# Revit family: НЕВАТОМ_Козырек VR-KP, версия 1
name_source: partatom
category: Оборудование
revit_build: Autodesk Revit 2017 (Build: 20170118_1100(x64)
units: mm (PartAtom-declared; Revit-internal decimal feet)

## family parameters
Всегда вертикально = Нет
На основе рабочей плоскости = Нет
Общий = Нет
При загрузке вырезать с полостями = Нет
Размер круглого соединителя = Использовать диаметр
Тип детали = Нормальный
Точка расчета площади = Нет

## types (12) — shared parameters
ADSK_Единица измерения = шт.
ADSK_Завод-изготовитель = НЕВАТОМ
ADSK_Количество = 1
ADSK_Материал наименование = сталь оцинкованная
Nevatom_URL = https://t.me
a = 5 мм
f1 = 5 мм
l = 60 мм

## per-type parameters (varying)
| type | A+60 | ADSK_Марка | ADSK_Наименование | L | l1 | А | С | С+60 |
| Козырек VR-KP 250-0,55/3000 | 205 мм | VR-KP 250-0,55/3000 | Козырек VR-KP 250-0,55/3000 | 350 мм | 100 мм | 145 мм | 390 мм | 450 мм |
| Козырек VR-KP 710-3/1000 | 457 мм | VR-KP 710-3/1000 | Козырек VR-KP 710-3/1000 | 650 мм | 186 мм | 397 мм | 990 мм | 1050 мм |
| Козырек VR-KP 280-0,75/3000 | 240 мм | VR-KP 280-0,75/3000 | Козырек VR-KP 280-0,75/3000 | 350 мм | 100 мм | 180 мм | 390 мм | 450 мм |
| Козырек VR-KP 315-1,5/3000 | 258 мм | VR-KP 315-1,5/3000 | Козырек VR-KP 315-1,5/3000 | 400 мм | 114 мм | 198 мм | 490 мм | 550 мм |
| Козырек VR-KP 355-2,2/3000 | 282 мм | VR-KP 355-2,2/3000 | Козырек VR-KP 355-2,2/3000 | 400 мм | 114 мм | 222 мм | 490 мм | 550 мм |
| Козырек VR-KP 400-0,55/1500 | 283 мм | VR-KP 400-0,55/1500 | Козырек VR-KP 400-0,55/1500 | 475 мм | 136 мм | 223 мм | 640 мм | 700 мм |
| Козырек VR-KP 450-0,75/1500 | 304 мм | VR-KP 400-0,55/1500 | Козырек VR-KP 400-0,55/1500 | 475 мм | 136 мм | 244 мм | 640 мм | 700 мм |
| Козырек VR-KP 500-0,37/1000 | 323 мм | VR-KP 500-0,37/1000 | Козырек VR-KP 500-0,37/1000 | 550 мм | 157 мм | 263 мм | 790 мм | 850 мм |
| Козырек VR-KP 500-1,5/1500 | 343 мм | VR-KP 500-1,5/1500 | Козырек VR-KP 500-1,5/1500 | 550 мм | 157 мм | 283 мм | 790 мм | 850 мм |
| Козырек VR-KP 560-1,1/1000 | 361 мм | VR-KP 560-1,1/1000 | Козырек VR-KP 560-1,1/1000 | 550 мм | 157 мм | 301 мм | 790 мм | 850 мм |
| Козырек VR-KP 630-1,5/1000 | 410 мм | VR-KP 630-1,5/1000 | Козырек VR-KP 630-1,5/1000 | 650 мм | 186 мм | 350 мм | 990 мм | 1050 мм |
| Козырек VR-KP 630-5,5/1500 | 440 мм | VR-KP 630-5,5/1500 | Козырек VR-KP 630-5,5/1500 | 650 мм | 186 мм | 380 мм | 990 мм | 1050 мм |
